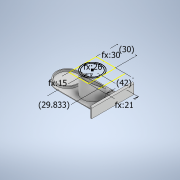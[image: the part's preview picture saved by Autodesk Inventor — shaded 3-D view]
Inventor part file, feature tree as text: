
AUTODESK INVENTOR PART (.ipt)
format: ipt  version: 2021 (Build 250183000, 183)  size: 976,896 bytes
history: native  units: in
note: dims shown in document units (in); Inventor stores cm internally (conversion verified against a paired STEP export)
features: extrude x10, sketch x9, fillet x3, chamfer x1
ambient origin geometry x8: Origin, YZ Plane, XZ Plane, XY Plane, X Axis, Y Axis, Z Axis, Center Point
bodies: Solid1 (feature_tree)
feature tree (23):
  extrude  "Extrusion1"  Depth=1.6535in
  extrude  "Extrusion2"  Depth=1.6535in
  sketch  "Sketch5"  dims[d5=1.1811in d6=0.0in d7=1.2598in d8=0.0in]
  extrude  "Extrusion3"  TaperAngle=0.0deg  [1 undecoded]
  chamfer  "Chamfer3"  Distance=1.2598in
  extrude  "Extrusion4"  Depth=0.5906in
  extrude  "Extrusion5"  Depth=1.1811in
  fillet  "Fillet3"  Radius=1.6535in
  extrude  "Extrusion8"  Depth=1.6535in
  extrude  "Extrusion9"  Depth=1.1811in
  extrude  "Extrusion10"  Depth=1.2402in
  fillet  "Fillet4"  Radius=0.8268in
  fillet  "Fillet5"  Radius=1.3386in
  extrude  "Extrusion11"  Depth=0.8268in
  extrude  "Extrusion12"  Depth=0.0394in
  sketch  "Sketch1"  dims[d0=3.3465in d1=1.6535in]
  sketch  "Sketch2"  dims[d2=0.0394in d3=0.0in d4=1.6535in]
  sketch  "Sketch6"  dims[d20=1.0236in d21=0.5906in]
  sketch  "Sketch9"  dims[d22=0.8268in d23=1.1811in d24=1.6535in]
  sketch  "Sketch10"  dims[d25=1.2598in d26=0.0in d30=1.6535in]
  sketch  "Sketch11"  dims[d31=1.2598in d32=45.0deg d34=1.1811in]
  sketch  "Sketch12"  dims[d35=1.2598in d36=0.0in d37=1.2402in d38=0.8268in d39=1.3386in]
  sketch  "Sketch13"  dims[d40=0.1181in d41=0.0in d42=0.8268in d49=0.0394in d50=2.5591in d51=0.0787in d52=0.0in d53=0.4528in d54=0.5906in d55=0.0in d56=0.4528in d58=0.0in d59=0.2362in d60=0.0in d61=0.2323in d62=0.0787in d63=1.1745in d64=0.6693in d65=0.2362in d66=0.315in d67=0.315in d68=0.1772in d69=0.1772in d70=0.0787in d71=0.0in d72=0.0in d73=0.0in d74=0.0in d75=0.0in d76=0.0787in d77=0.0in]
note: 1 required parameter value undecoded (feature->parameter linkage not recoverable at this tier; creation-order binding heuristic only, values carry confidence <= 0.55)
